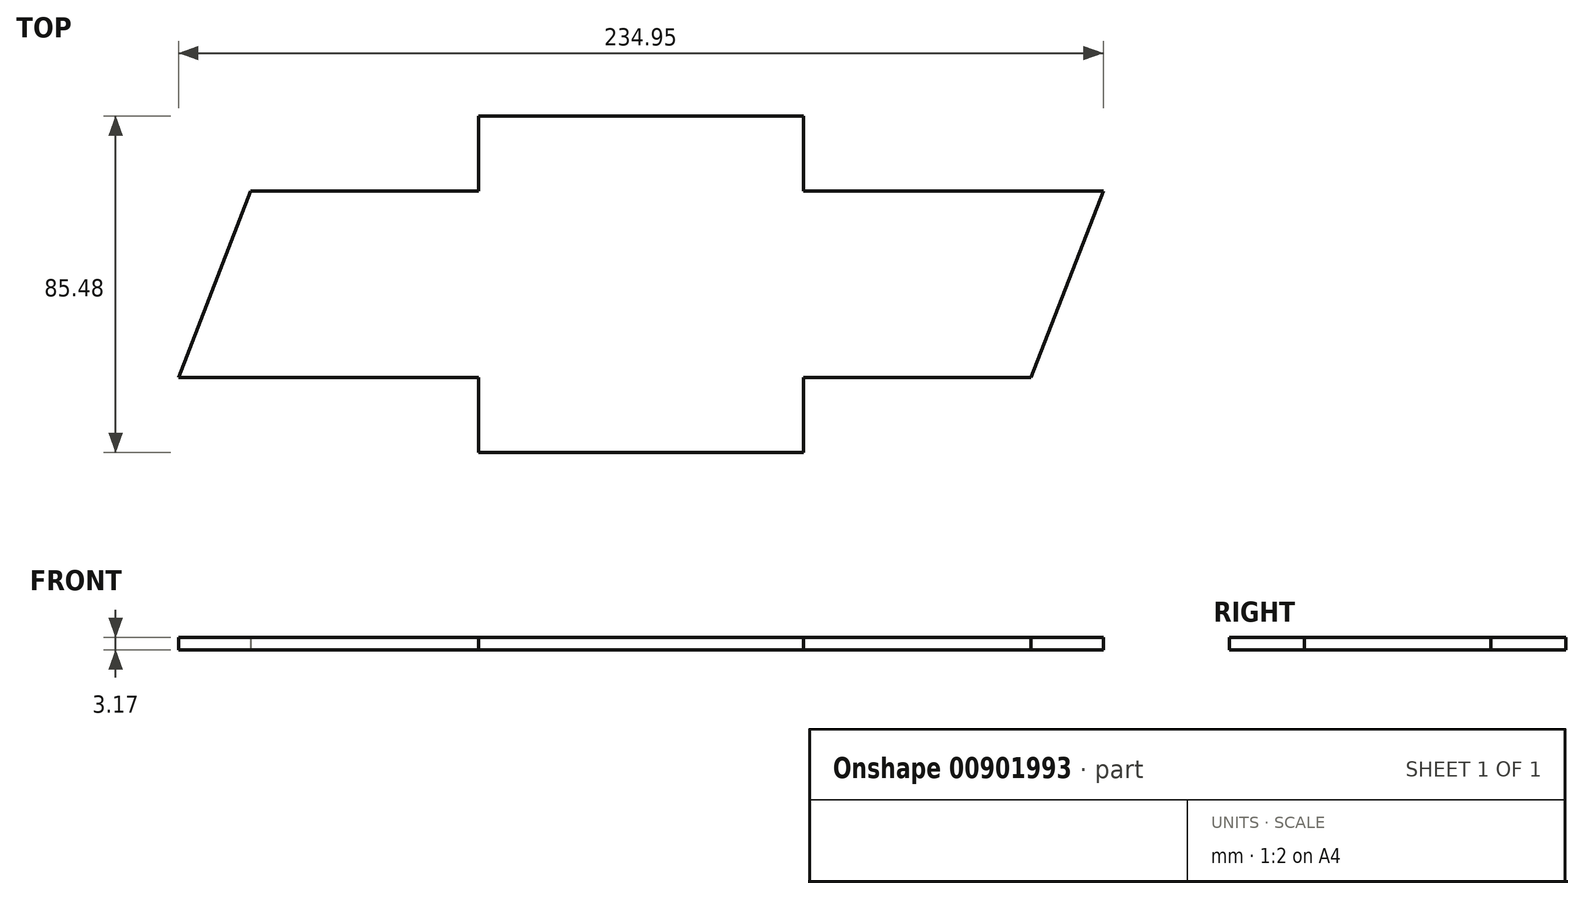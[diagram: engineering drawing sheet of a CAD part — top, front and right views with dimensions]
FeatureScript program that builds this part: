
annotation { "Feature Type Name" : "Feature", "Feature Type Description" : "" }
export const myFeature = defineFeature(function(context is Context, id is Id, definition is map)
    precondition{}
    {
        {
            var Q0;
            Q0=qCreatedBy(makeId("Top.planeOp"),FACE);
            var sketch = newSketch(context, id + "F0", { "sketchPlane" : qUnion([Q0])});
            skLineSegment(sketch, "E0", {"start": v(0, 0) * mm, "end": v(82.55, 0) * mm});
            skLineSegment(sketch, "E1", {"start": v(82.55, 0) * mm, "end": v(82.55, -19.05) * mm});
            skLineSegment(sketch, "E2", {"start": v(82.55, -19.05) * mm, "end": v(158.75, -19.05) * mm});
            skLineSegment(sketch, "E3", {"start": v(158.75, -19.05) * mm, "end": v(140.42, -66.43) * mm});
            skLineSegment(sketch, "E4", {"start": v(0, 0) * mm, "end": v(0, -19.05) * mm});
            skLineSegment(sketch, "E5", {"start": v(0, -19.05) * mm, "end": v(-57.87, -19.05) * mm});
            skLineSegment(sketch, "E6", {"start": v(-57.87, -19.05) * mm, "end": v(-76.2, -66.43) * mm});
            skLineSegment(sketch, "E7", {"start": v(-76.2, -66.43) * mm, "end": v(0, -66.43) * mm});
            skLineSegment(sketch, "E8", {"start": v(0, -66.43) * mm, "end": v(0, -85.48) * mm});
            skLineSegment(sketch, "E9", {"start": v(0, -85.48) * mm, "end": v(82.55, -85.48) * mm});
            skLineSegment(sketch, "E10", {"start": v(82.55, -85.48) * mm, "end": v(82.55, -66.43) * mm});
            skLineSegment(sketch, "E11", {"start": v(82.55, -66.43) * mm, "end": v(140.42, -66.43) * mm});
            skSolve(sketch);
        }
        {
            var Q0;
            Q0=makeQuery(id+"F0.imprint","IMPRINT",FACE,{"disambiguationData":[TD([[makeQuery(id+"F0.imprint","IMPRINT",EDGE,{"derivedFrom":sQuery(id+"F0.wireOp",EDGE,"E0")}),-1.0]])]});
            var Q1;
            Q1=sQuery(id+"F0.wireOp",EDGE,"E7");
            var Q2;
            Q2=sQuery(id+"F0.wireOp",EDGE,"E6");
            var Q3;
            Q3=sQuery(id+"F0.wireOp",EDGE,"E5");
            var Q4;
            Q4=sQuery(id+"F0.wireOp",EDGE,"E4");
            var Q5;
            Q5=sQuery(id+"F0.wireOp",EDGE,"E0");
            var Q6;
            Q6=sQuery(id+"F0.wireOp",EDGE,"E1");
            var Q7;
            Q7=sQuery(id+"F0.wireOp",EDGE,"E2");
            var Q8;
            Q8=sQuery(id+"F0.wireOp",EDGE,"E3");
            var Q9;
            Q9=sQuery(id+"F0.wireOp",EDGE,"E11");
            var Q10;
            Q10=sQuery(id+"F0.wireOp",EDGE,"E9");
            var Q11;
            Q11=sQuery(id+"F0.wireOp",EDGE,"E8");
            var Q12;
            Q12=sQuery(id+"F0.wireOp",EDGE,"E10");
            extrude(context, id + "F1", {"entities" : qUnion([Q0]), "surfaceEntities" : qUnion([Q1, Q2, Q3, Q4, Q5, Q6, Q7, Q8, Q9, Q10, Q11, Q12]), "depth" : 3.17 * mm, "offsetDistance" : 25.4 * mm});
        }
        {
            var Q0;
            Q0=makeQuery(id+"F1.opExtrude","CAP_FACE",FACE,{"disambiguationData":[OSD([sQuery(id+"F0.wireOp",EDGE,"E0"),sQuery(id+"F0.wireOp",EDGE,"E1"),sQuery(id+"F0.wireOp",EDGE,"E2"),sQuery(id+"F0.wireOp",EDGE,"E3"),sQuery(id+"F0.wireOp",EDGE,"E4"),sQuery(id+"F0.wireOp",EDGE,"E5"),sQuery(id+"F0.wireOp",EDGE,"E6"),sQuery(id+"F0.wireOp",EDGE,"E7"),sQuery(id+"F0.wireOp",EDGE,"E8"),sQuery(id+"F0.wireOp",EDGE,"E9"),sQuery(id+"F0.wireOp",EDGE,"E10"),sQuery(id+"F0.wireOp",EDGE,"E11")])],"isStart":false});
            var Q1;
            Q1=sQuery(id+"F0.wireOp",EDGE,"E6");
            var Q2;
            Q2=sQuery(id+"F0.wireOp",EDGE,"E7");
            var Q3;
            Q3=sQuery(id+"F0.wireOp",EDGE,"E5");
            var Q4;
            Q4=sQuery(id+"F0.wireOp",EDGE,"E4");
            var Q5;
            Q5=sQuery(id+"F0.wireOp",EDGE,"E0");
            var Q6;
            Q6=sQuery(id+"F0.wireOp",EDGE,"E1");
            var Q7;
            Q7=sQuery(id+"F0.wireOp",EDGE,"E2");
            var Q8;
            Q8=sQuery(id+"F0.wireOp",EDGE,"E3");
            var Q9;
            Q9=sQuery(id+"F0.wireOp",EDGE,"E11");
            var Q10;
            Q10=sQuery(id+"F0.wireOp",EDGE,"E9");
            var Q11;
            Q11=sQuery(id+"F0.wireOp",EDGE,"E10");
            var Q12;
            Q12=sQuery(id+"F0.wireOp",EDGE,"E8");
            extrude(context, id + "F2", {"entities" : qUnion([Q0]), "bodyType" : ToolBodyType.SURFACE, "surfaceEntities" : qUnion([Q1, Q2, Q3, Q4, Q5, Q6, Q7, Q8, Q9, Q10, Q11, Q12]), "depth" : 50.8 * mm, "offsetDistance" : 25.4 * mm});
        }
    });
